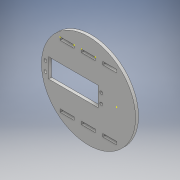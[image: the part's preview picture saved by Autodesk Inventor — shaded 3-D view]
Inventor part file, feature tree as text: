
AUTODESK INVENTOR PART (.ipt)
format: ipt  version: 2018 (Build 220112000, 112)  size: 153,088 bytes
history: native  units: mm
features: sketch x5, extrude x4, other x1
ambient origin geometry x8: Origin, YZ Plane, XZ Plane, XY Plane, X Axis, Y Axis, Z Axis, Center Point
bodies: Body1 (feature_tree)
feature tree (10):
  other  "Sólido1"
  extrude  "Extrusión1"  Depth=3.0mm
  extrude  "Extrusión2"  Depth=10.0mm
  extrude  "Extrusión3"  Depth=50.0mm
  extrude  "Extrusión4"  [1 undecoded]
  sketch  "Boceto5"
  sketch  "Boceto1"  dims[d19=3.0mm d20=0.0mm d23=7.0mm]
  sketch  "Boceto2"  dims[d24=10.0mm d25=0.0mm d26=9.0mm]
  sketch  "Boceto3"  dims[d27=10.0mm d28=0.0mm d32=50.0mm]
  sketch  "Boceto4"  dims[d36=3.0mm d37=0.0mm]
note: 1 required parameter value undecoded (feature->parameter linkage not recoverable at this tier; creation-order binding heuristic only, values carry confidence <= 0.55)
